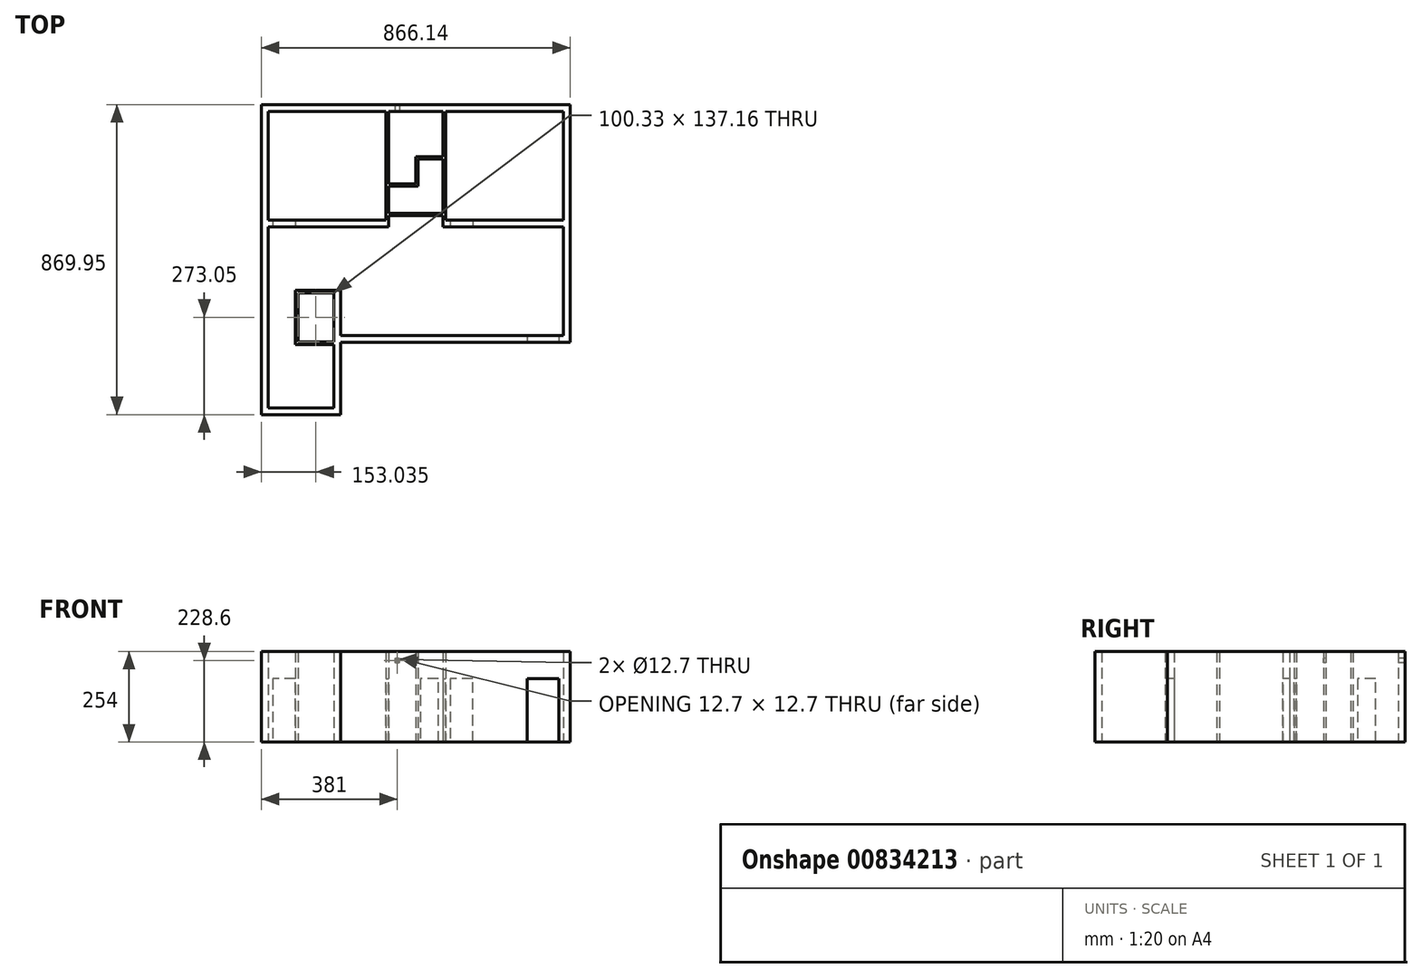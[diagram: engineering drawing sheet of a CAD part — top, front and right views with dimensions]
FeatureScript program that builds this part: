
annotation { "Feature Type Name" : "Feature", "Feature Type Description" : "" }
export const myFeature = defineFeature(function(context is Context, id is Id, definition is map)
    precondition{}
    {
        {
            var Q0;
            Q0=qCreatedBy(makeId("Top.planeOp"),FACE);
            var sketch = newSketch(context, id + "F0", { "sketchPlane" : qUnion([Q0])});
            skLineSegment(sketch, "E0.bottom", {"start": v(0, 0) * mm, "end": v(330.2, 0) * mm});
            skLineSegment(sketch, "E0.top", {"start": v(0, -304.8) * mm, "end": v(330.2, -304.8) * mm});
            skLineSegment(sketch, "E0.left", {"start": v(0, 0) * mm, "end": v(0, -304.8) * mm});
            skLineSegment(sketch, "E0.right", {"start": v(330.2, 0) * mm, "end": v(330.2, -304.8) * mm});
            skLineSegment(sketch, "E1.bottom", {"start": v(337.82, 0) * mm, "end": v(490.22, 0) * mm});
            skLineSegment(sketch, "E2.bottom", {"start": v(497.84, 0) * mm, "end": v(828.04, 0) * mm});
            skLineSegment(sketch, "E2.top", {"start": v(497.84, -304.8) * mm, "end": v(828.04, -304.8) * mm});
            skLineSegment(sketch, "E2.left", {"start": v(497.84, 0) * mm, "end": v(497.84, -304.8) * mm});
            skLineSegment(sketch, "E2.right", {"start": v(828.04, 0) * mm, "end": v(828.04, -304.8) * mm});
            skPoint(sketch, "E3", {"position": v(-19.05, 19.05) * mm});
            skLineSegment(sketch, "E4", {"start": v(-19.05, 19.05) * mm, "end": v(847.1, 19.05) * mm});
            skLineSegment(sketch, "E5", {"start": v(490.22, 0) * mm, "end": v(497.84, 0) * mm});
            skLineSegment(sketch, "E6", {"start": v(-19.05, 19.05) * mm, "end": v(-19.05, -323.85) * mm});
            skPoint(sketch, "E7", {"position": v(0, -323.85) * mm});
            skLineSegment(sketch, "E8", {"start": v(0, -323.85) * mm, "end": v(337.82, -323.85) * mm});
            skLineSegment(sketch, "E9", {"start": v(490.22, -323.85) * mm, "end": v(828.04, -323.85) * mm});
            skLineSegment(sketch, "E10", {"start": v(0, -323.85) * mm, "end": v(0, -831.85) * mm});
            skPoint(sketch, "E11", {"position": v(76.2, -501.65) * mm});
            skLineSegment(sketch, "E12", {"start": v(76.2, -501.65) * mm, "end": v(203.2, -501.65) * mm});
            skLineSegment(sketch, "E13", {"start": v(76.2, -654.05) * mm, "end": v(76.2, -501.65) * mm});
            skLineSegment(sketch, "E14", {"start": v(0, -831.85) * mm, "end": v(184.15, -831.85) * mm});
            skLineSegment(sketch, "E15", {"start": v(-19.05, -323.85) * mm, "end": v(-19.05, -850.9) * mm});
            skLineSegment(sketch, "E16", {"start": v(-19.05, -850.9) * mm, "end": v(203.2, -850.9) * mm});
            skLineSegment(sketch, "E17", {"start": v(203.2, -850.9) * mm, "end": v(203.2, -501.65) * mm});
            skLineSegment(sketch, "E18", {"start": v(184.15, -831.85) * mm, "end": v(184.15, -509.27) * mm});
            skLineSegment(sketch, "E19", {"start": v(184.15, -509.27) * mm, "end": v(83.82, -509.27) * mm});
            skLineSegment(sketch, "E20", {"start": v(83.82, -509.27) * mm, "end": v(83.82, -646.43) * mm});
            skLineSegment(sketch, "E21", {"start": v(83.82, -646.43) * mm, "end": v(184.15, -646.43) * mm});
            skPoint(sketch, "E22", {"position": v(203.2, -628.65) * mm});
            skLineSegment(sketch, "E23", {"start": v(203.2, -628.65) * mm, "end": v(828.04, -628.65) * mm});
            skLineSegment(sketch, "E24", {"start": v(828.04, -323.85) * mm, "end": v(828.04, -628.65) * mm});
            skPoint(sketch, "E25", {"position": v(847.1, -647.7) * mm});
            skLineSegment(sketch, "E26", {"start": v(847.1, 19.05) * mm, "end": v(847.1, -647.7) * mm});
            skLineSegment(sketch, "E27", {"start": v(847.1, -647.7) * mm, "end": v(203.2, -647.7) * mm});
            skLineSegment(sketch, "E28.bottom", {"start": v(828.04, -323.85) * mm, "end": v(675.64, -323.85) * mm});
            skLineSegment(sketch, "E28.left", {"start": v(828.04, -323.85) * mm, "end": v(828.04, -450.85) * mm});
            skLineSegment(sketch, "E29.bottom", {"start": v(828.04, -323.85) * mm, "end": v(668.02, -323.85) * mm});
            skLineSegment(sketch, "E29.left", {"start": v(828.04, -323.85) * mm, "end": v(828.04, -458.47) * mm});
            skLineSegment(sketch, "E30", {"start": v(76.2, -654.05) * mm, "end": v(184.15, -654.05) * mm});
            skLineSegment(sketch, "E31", {"start": v(337.82, 0) * mm, "end": v(337.82, -203.2) * mm});
            skLineSegment(sketch, "E32", {"start": v(337.82, -203.2) * mm, "end": v(414.02, -203.2) * mm});
            skLineSegment(sketch, "E33", {"start": v(414.02, -203.2) * mm, "end": v(414.02, -127) * mm});
            skLineSegment(sketch, "E34", {"start": v(414.02, -127) * mm, "end": v(490.22, -127) * mm});
            skLineSegment(sketch, "E35", {"start": v(490.22, -127) * mm, "end": v(490.22, 0) * mm});
            skLineSegment(sketch, "E36", {"start": v(337.82, -323.85) * mm, "end": v(337.82, -292.1) * mm});
            skLineSegment(sketch, "E37", {"start": v(337.82, -292.1) * mm, "end": v(490.22, -292.1) * mm});
            skLineSegment(sketch, "E38", {"start": v(490.22, -292.1) * mm, "end": v(490.22, -323.85) * mm});
            skPoint(sketch, "E39", {"position": v(337.82, -209.55) * mm});
            skLineSegment(sketch, "E40", {"start": v(337.82, -209.55) * mm, "end": v(420.37, -209.55) * mm});
            skLineSegment(sketch, "E41", {"start": v(420.37, -209.55) * mm, "end": v(420.37, -133.35) * mm});
            skLineSegment(sketch, "E42", {"start": v(420.37, -133.35) * mm, "end": v(490.22, -133.35) * mm});
            skLineSegment(sketch, "E43", {"start": v(490.22, -133.35) * mm, "end": v(490.22, -285.75) * mm});
            skLineSegment(sketch, "E44", {"start": v(490.22, -285.75) * mm, "end": v(337.82, -285.75) * mm});
            skLineSegment(sketch, "E45", {"start": v(337.82, -285.75) * mm, "end": v(337.82, -209.55) * mm});
            skSolve(sketch);
        }
        {
            var Q0;
            Q0=makeQuery(id+"F0.imprint","IMPRINT",FACE,{"disambiguationData":[TD([[makeQuery(id+"F0.imprint","IMPRINT",EDGE,{"derivedFrom":sQuery(id+"F0.wireOp",EDGE,"E0.bottom")}),1.0]])]});
            extrude(context, id + "F1", {"entities" : qUnion([Q0]), "depth" : 254 * mm, "offsetDistance" : 25.4 * mm});
        }
        {
            var Q0;
            Q0=makeQuery(id+"F1.opExtrude","SWEPT_FACE",FACE,{"disambiguationData":[OSD([sQuery(id+"F0.wireOp",EDGE,"E37")])]});
            var sketch = newSketch(context, id + "F2", { "sketchPlane" : qUnion([Q0])});
            skLineSegment(sketch, "E46", {"start": v(477.52, 0) * mm, "end": v(477.52, 177.8) * mm});
            skLineSegment(sketch, "E47", {"start": v(477.52, 177.8) * mm, "end": v(426.72, 177.8) * mm});
            skLineSegment(sketch, "E48", {"start": v(426.72, 177.8) * mm, "end": v(426.72, 0) * mm});
            skSolve(sketch);
        }
        {
            var Q0;
            {var subQ0=sQuery(id+"F2.wireOp",EDGE,"E46");Q0=makeQuery(id+"F2.imprint","IMPRINT",FACE,{"disambiguationData":[TD([[makeQuery(id+"F2.imprint","IMPRINT",EDGE,{"derivedFrom":subQ0}),1.0]])]});}
            extrude(context, id + "F3", {"entities" : qUnion([Q0]), "operationType" : NewBodyOperationType.REMOVE, "oppositeDirection" : true, "depth" : 25.4 * mm, "offsetDistance" : 25.4 * mm});
        }
        {
            var Q0;
            Q0=makeQuery(id+"F1.opExtrude","SWEPT_FACE",FACE,{"disambiguationData":[OSD([sQuery(id+"F0.wireOp",EDGE,"E2.left")])]});
            var sketch = newSketch(context, id + "F4", { "sketchPlane" : qUnion([Q0])});
            skLineSegment(sketch, "E49", {"start": v(-114.3, 0) * mm, "end": v(-114.3, 177.8) * mm});
            skLineSegment(sketch, "E50", {"start": v(-114.3, 177.8) * mm, "end": v(-63.5, 177.8) * mm});
            skLineSegment(sketch, "E51", {"start": v(-63.5, 177.8) * mm, "end": v(-63.5, 0) * mm});
            skSolve(sketch);
        }
        {
            var Q0;
            {var subQ0=sQuery(id+"F4.wireOp",EDGE,"E49");Q0=makeQuery(id+"F4.imprint","IMPRINT",FACE,{"disambiguationData":[TD([[makeQuery(id+"F4.imprint","IMPRINT",EDGE,{"derivedFrom":subQ0}),-1.0]])]});}
            extrude(context, id + "F5", {"entities" : qUnion([Q0]), "operationType" : NewBodyOperationType.REMOVE, "oppositeDirection" : true, "depth" : 177.8 * mm, "offsetDistance" : 25.4 * mm});
        }
        {
            var Q0;
            Q0=makeQuery(id+"F1.opExtrude","SWEPT_FACE",FACE,{"disambiguationData":[OSD([sQuery(id+"F0.wireOp",EDGE,"E8")])]});
            var sketch = newSketch(context, id + "F6", { "sketchPlane" : qUnion([Q0])});
            skLineSegment(sketch, "E52", {"start": v(12.7, 0) * mm, "end": v(12.7, 177.8) * mm});
            skLineSegment(sketch, "E53", {"start": v(12.7, 177.8) * mm, "end": v(76.2, 177.8) * mm});
            skLineSegment(sketch, "E54", {"start": v(76.2, 177.8) * mm, "end": v(76.2, 0) * mm});
            skSolve(sketch);
        }
        {
            var Q0;
            {var subQ0=sQuery(id+"F6.wireOp",EDGE,"E52");Q0=makeQuery(id+"F6.imprint","IMPRINT",FACE,{"disambiguationData":[TD([[makeQuery(id+"F6.imprint","IMPRINT",EDGE,{"derivedFrom":subQ0}),-1.0]])]});}
            extrude(context, id + "F7", {"entities" : qUnion([Q0]), "operationType" : NewBodyOperationType.REMOVE, "oppositeDirection" : true, "depth" : 25.4 * mm, "offsetDistance" : 25.4 * mm});
        }
        {
            var Q0;
            Q0=makeQuery(id+"F1.opExtrude","SWEPT_FACE",FACE,{"disambiguationData":[OSD([sQuery(id+"F0.wireOp",EDGE,"E9"),sQuery(id+"F0.wireOp",EDGE,"E29.bottom")])]});
            var sketch = newSketch(context, id + "F8", { "sketchPlane" : qUnion([Q0])});
            skLineSegment(sketch, "E55", {"start": v(510.54, 0) * mm, "end": v(510.54, 177.8) * mm});
            skLineSegment(sketch, "E56", {"start": v(510.54, 177.8) * mm, "end": v(574.04, 177.8) * mm});
            skLineSegment(sketch, "E57", {"start": v(574.04, 177.8) * mm, "end": v(574.04, 0) * mm});
            skSolve(sketch);
        }
        {
            var Q0;
            {var subQ0=sQuery(id+"F8.wireOp",EDGE,"E55");Q0=makeQuery(id+"F8.imprint","IMPRINT",FACE,{"disambiguationData":[TD([[makeQuery(id+"F8.imprint","IMPRINT",EDGE,{"derivedFrom":subQ0}),-1.0]])]});}
            extrude(context, id + "F9", {"entities" : qUnion([Q0]), "operationType" : NewBodyOperationType.REMOVE, "oppositeDirection" : true, "depth" : 25.4 * mm, "offsetDistance" : 25.4 * mm});
        }
        {
            var Q0;
            Q0=makeQuery(id+"F1.opExtrude","SWEPT_FACE",FACE,{"disambiguationData":[OSD([sQuery(id+"F0.wireOp",EDGE,"E27")])]});
            var sketch = newSketch(context, id + "F10", { "sketchPlane" : qUnion([Q0])});
            skLineSegment(sketch, "E58", {"start": v(815.34, 0) * mm, "end": v(815.34, 177.8) * mm});
            skLineSegment(sketch, "E59", {"start": v(815.34, 177.8) * mm, "end": v(726.44, 177.8) * mm});
            skLineSegment(sketch, "E60", {"start": v(726.44, 177.8) * mm, "end": v(726.44, 0) * mm});
            skSolve(sketch);
        }
        {
            var Q0;
            {var subQ0=sQuery(id+"F10.wireOp",EDGE,"E58");Q0=makeQuery(id+"F10.imprint","IMPRINT",FACE,{"disambiguationData":[TD([[makeQuery(id+"F10.imprint","IMPRINT",EDGE,{"derivedFrom":subQ0}),1.0]])]});}
            extrude(context, id + "F11", {"entities" : qUnion([Q0]), "operationType" : NewBodyOperationType.REMOVE, "oppositeDirection" : true, "depth" : 25.4 * mm, "offsetDistance" : 25.4 * mm});
        }
        {
            var Q0;
            Q0=makeQuery(id+"F1.opExtrude","SWEPT_FACE",FACE,{"disambiguationData":[OSD([sQuery(id+"F0.wireOp",EDGE,"E40")])]});
            var sketch = newSketch(context, id + "F12", { "sketchPlane" : qUnion([Q0])});
            skPoint(sketch, "E61", {"position": v(361.95, 228.6) * mm});
            skCircle(sketch, "E62", {"center": v(361.95, 228.6) * mm, "radius": 6.35 * mm});
            skSolve(sketch);
        }
        {
            var Q0;
            Q0=makeQuery(id+"F12.imprint","IMPRINT",FACE,{"disambiguationData":[TD([[makeQuery(id+"F12.imprint","IMPRINT",EDGE,{"derivedFrom":sQuery(id+"F12.wireOp",EDGE,"E62")}),1.0]])]});
            extrude(context, id + "F13", {"entities" : qUnion([Q0]), "operationType" : NewBodyOperationType.REMOVE, "oppositeDirection" : true, "depth" : 228.6 * mm, "offsetDistance" : 25.4 * mm});
        }
    });
